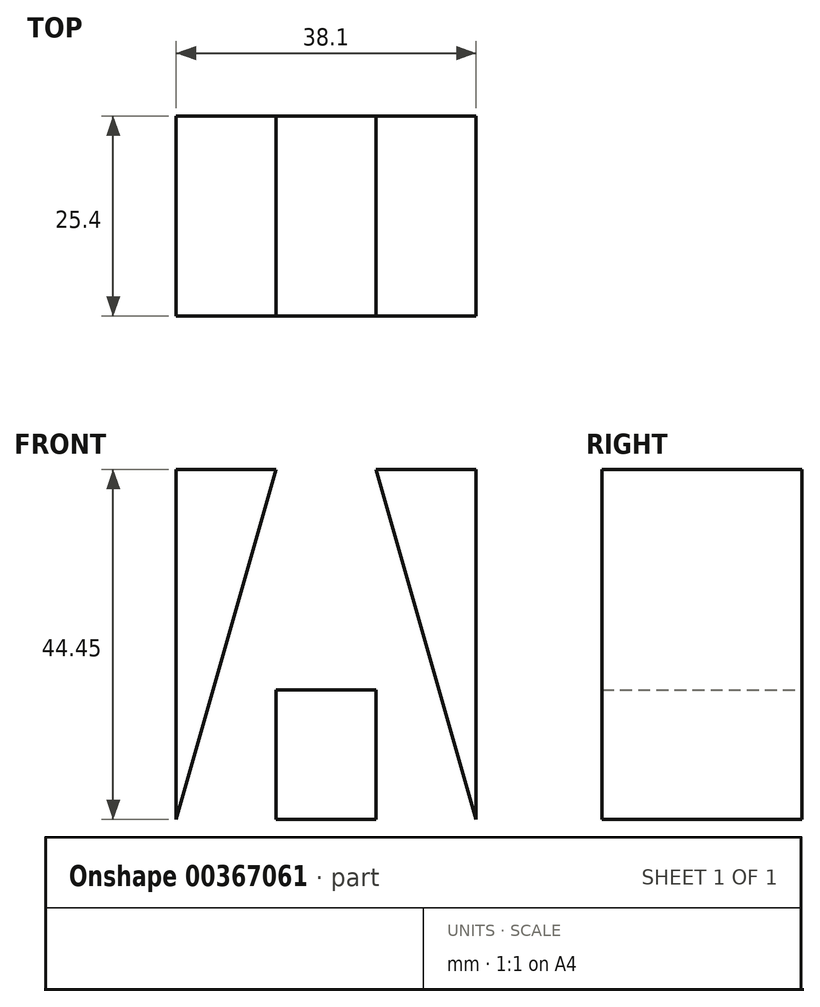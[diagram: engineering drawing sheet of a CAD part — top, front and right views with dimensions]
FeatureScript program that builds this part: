
annotation { "Feature Type Name" : "Feature", "Feature Type Description" : "" }
export const myFeature = defineFeature(function(context is Context, id is Id, definition is map)
    precondition{}
    {
        {
            var Q0;
            Q0=qCreatedBy(makeId("Front.planeOp"),FACE);
            var sketch = newSketch(context, id + "F0", { "sketchPlane" : qUnion([Q0])});
            skLineSegment(sketch, "E0", {"start": v(0, 0) * mm, "end": v(38.1, 0) * mm});
            skLineSegment(sketch, "E1", {"start": v(38.1, 0) * mm, "end": v(38.1, 44.45) * mm});
            skLineSegment(sketch, "E2", {"start": v(38.1, 44.45) * mm, "end": v(0, 44.45) * mm});
            skLineSegment(sketch, "E3", {"start": v(0, 44.45) * mm, "end": v(0, 0) * mm});
            skSolve(sketch);
        }
        {
            var Q0;
            Q0 = qSketchRegion(id + "F0", true);
            extrude(context, id + "F1", {"entities" : qUnion([Q0]), "depth" : 25.4 * mm});
        }
        {
            var Q0;
            Q0=qCreatedBy(makeId("Front.planeOp"),FACE);
            var sketch = newSketch(context, id + "F2", { "sketchPlane" : qUnion([Q0])});
            skLineSegment(sketch, "E4", {"start": v(12.7, 44.45) * mm, "end": v(25.4, 44.45) * mm});
            skLineSegment(sketch, "E5", {"start": v(38.1, 0) * mm, "end": v(25.4, 0) * mm});
            skLineSegment(sketch, "E6", {"start": v(25.4, 0) * mm, "end": v(25.4, 16.42) * mm});
            skLineSegment(sketch, "E7", {"start": v(12.7, 16.42) * mm, "end": v(12.7, 0) * mm});
            skLineSegment(sketch, "E8", {"start": v(12.7, 0) * mm, "end": v(0, 0) * mm});
            skLineSegment(sketch, "E9", {"start": v(12.7, 16.42) * mm, "end": v(25.4, 16.42) * mm});
            skLineSegment(sketch, "E10", {"start": v(0, 0) * mm, "end": v(12.7, 44.45) * mm});
            skLineSegment(sketch, "E11", {"start": v(25.4, 44.45) * mm, "end": v(38.1, 0) * mm});
            skSolve(sketch);
        }
        {
            var Q0;
            Q0 = qSketchRegion(id + "F2", true);
            extrude(context, id + "F3", {"entities" : qUnion([Q0]), "depth" : 25.4 * mm});
        }
        {
            var Q0;
            Q0 = qSketchRegion(id + "F2", true);
            extrude(context, id + "F4", {"entities" : qUnion([Q0]), "operationType" : NewBodyOperationType.REMOVE, "depth" : 25.4 * mm});
        }
    });
